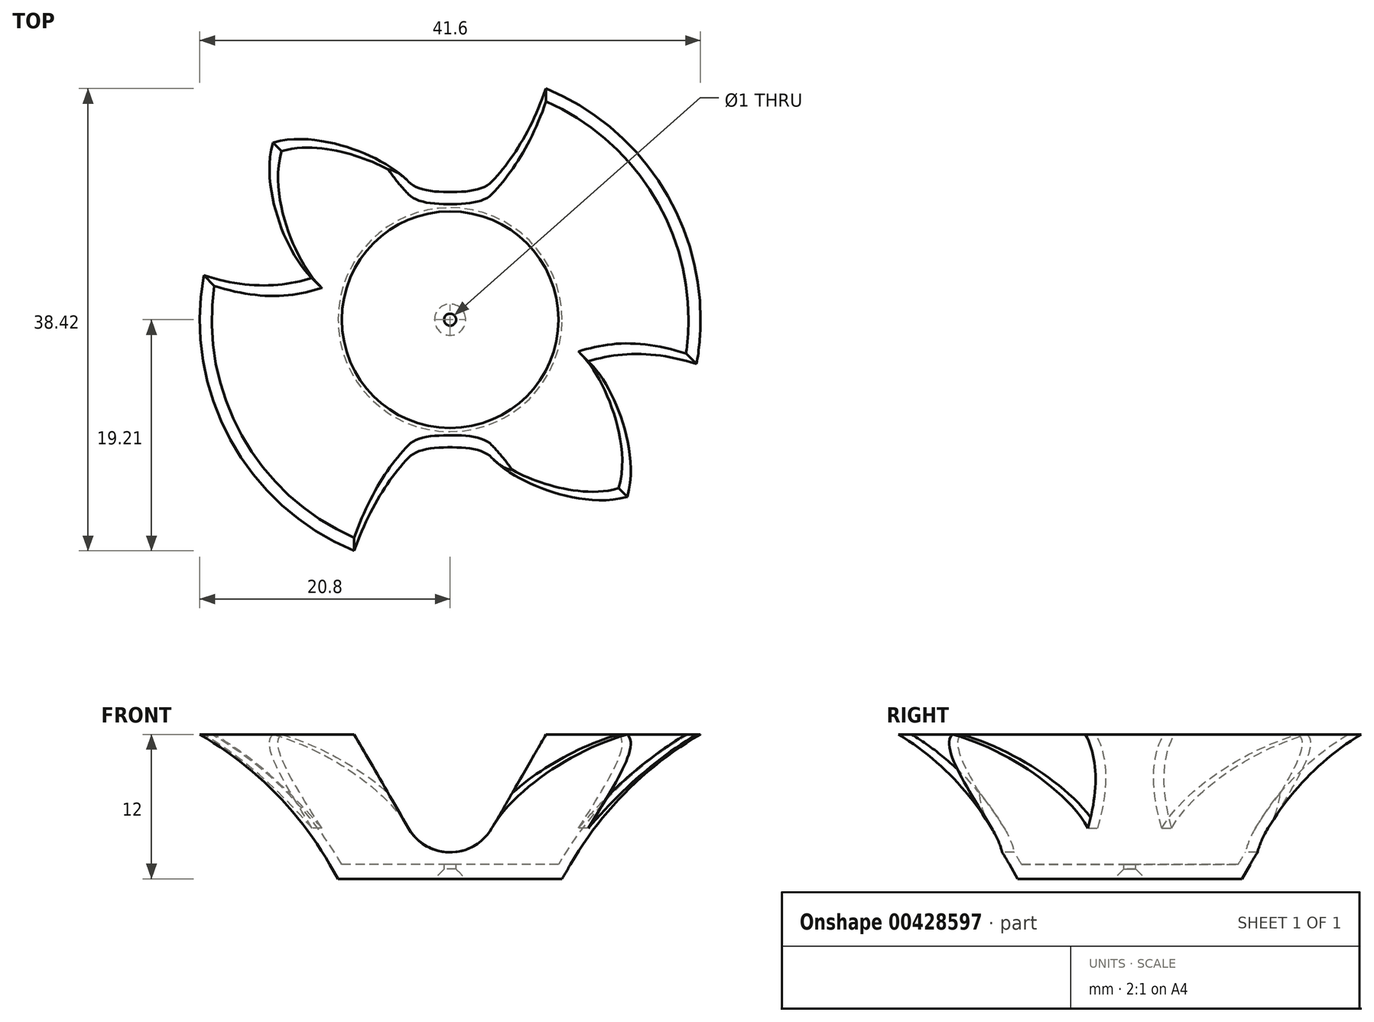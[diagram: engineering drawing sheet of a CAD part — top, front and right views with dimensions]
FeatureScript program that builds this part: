
annotation { "Feature Type Name" : "Feature", "Feature Type Description" : "" }
export const myFeature = defineFeature(function(context is Context, id is Id, definition is map)
    precondition{}
    {
        {
            var Q0;
            Q0=qCreatedBy(makeId("Front.planeOp"),FACE);
            var sketch = newSketch(context, id + "F0", { "sketchPlane" : qUnion([Q0])});
            skLineSegment(sketch, "E0", {"start": v(1.3, 0) * mm, "end": v(9.3, 0) * mm});
            skLineSegment(sketch, "E1", {"start": v(9.3, 0) * mm, "end": v(10, 1.2) * mm});
            skLineSegment(sketch, "E2", {"start": v(9, 1.2) * mm, "end": v(0.5, 1.2) * mm});
            skLineSegment(sketch, "E3", {"start": v(0.5, 1.2) * mm, "end": v(0.5, 0.8) * mm});
            skLineSegment(sketch, "E4", {"start": v(0.5, 0.8) * mm, "end": v(1.3, 0) * mm});
            skArc(sketch, "E5", {"start": v(20.8, 12) * mm, "mid": v(14.69, 7.31) * mm, "end": v(10, 1.2) * mm});
            skArc(sketch, "E6", {"start": v(19.8, 12) * mm, "mid": v(13.69, 7.31) * mm, "end": v(9, 1.2) * mm});
            skLineSegment(sketch, "E7", {"start": v(19.8, 12) * mm, "end": v(0, 0.57) * mm, "construction": true});
            skLineSegment(sketch, "E8", {"start": v(0, 0.57) * mm, "end": v(0, 0) * mm, "construction": true});
            skLineSegment(sketch, "E9", {"start": v(19.8, 12) * mm, "end": v(20.8, 12) * mm});
            skLineSegment(sketch, "E10", {"start": v(9, 1.2) * mm, "end": v(8.3, 0) * mm, "construction": true});
            skSolve(sketch);
        }
        {
            var Q0;
            Q0 = qSketchRegion(id + "F0", true);
            var Q1;
            Q1=sQuery(id+"F0.wireOp",EDGE,"E8");
            revolve(context, id + "F1", {"entities" : qUnion([Q0]), "axis" : qUnion([Q1]), "revolveType" : RevolveType.FULL});
        }
        {
            var Q0;
            Q0=qCreatedBy(makeId("Front.planeOp"),FACE);
            var sketch = newSketch(context, id + "F2", { "sketchPlane" : qUnion([Q0])});
            skArc(sketch, "E11", {"start": v(-3.46, 4.2) * mm, "mid": v(0, 2.2) * mm, "end": v(3.46, 4.2) * mm});
            skPoint(sketch, "E12", {"position": v(0, 12) * mm});
            skLineSegment(sketch, "E13", {"start": v(-3.46, 4.2) * mm, "end": v(-7.97, 12) * mm});
            skLineSegment(sketch, "E14", {"start": v(-7.97, 12) * mm, "end": v(7.97, 12) * mm});
            skLineSegment(sketch, "E15", {"start": v(7.97, 12) * mm, "end": v(3.46, 4.2) * mm});
            skSolve(sketch);
        }
        {
            var Q0;
            Q0 = qSketchRegion(id + "F2", true);
            extrude(context, id + "F3", {"entities" : qUnion([Q0]), "operationType" : NewBodyOperationType.REMOVE, "endBound" : BoundingType.THROUGH_ALL, "oppositeDirection" : true, "depth" : 25 * mm, "hasSecondDirection" : true, "secondDirectionBound" : SecondDirectionBoundingType.THROUGH_ALL, "secondDirectionOppositeDirection" : false, "secondDirectionDepth" : 25 * mm});
        }
        {
            var Q0;
            Q0=qCreatedBy(makeId("Front.planeOp"),FACE);
            var sketch = newSketch(context, id + "F4", { "sketchPlane" : qUnion([Q0])});
            skLineSegment(sketch, "E16", {"start": v(0, 0) * mm, "end": v(0, 50) * mm});
            skSolve(sketch);
        }
        {
            var Q0;
            Q0=sQuery(id+"F4.wireOp",EDGE,"E16");
            var Q1;
            Q1=qCreatedBy(makeId("Front.planeOp"),FACE);
            cPlane(context, id + "F5", {"entities" : qUnion([Q0, Q1]), "cplaneType" : CPlaneType.LINE_ANGLE, "offset" : 25 * mm, "angle" : 45 * degree, "width" : 150 * mm, "height" : 150 * mm});
        }
        {
            var Q0;
            Q0=qCreatedBy(id+"F5.planeOp",FACE);
            var sketch = newSketch(context, id + "F6", { "sketchPlane" : qUnion([Q0])});
            skArc(sketch, "E17", {"start": v(0, 12) * mm, "mid": v(-4.15, 9.06) * mm, "end": v(-5.66, 4.2) * mm});
            skArc(sketch, "E18", {"start": v(5.66, 4.2) * mm, "mid": v(4.15, 9.06) * mm, "end": v(0, 12) * mm});
            skLineSegment(sketch, "E19", {"start": v(5.66, 4.2) * mm, "end": v(15, 15.94) * mm});
            skLineSegment(sketch, "E20", {"start": v(15, 15.94) * mm, "end": v(0, 15.94) * mm});
            skLineSegment(sketch, "E21", {"start": v(0, 15.94) * mm, "end": v(-15, 15.94) * mm});
            skLineSegment(sketch, "E22", {"start": v(-15, 15.94) * mm, "end": v(-5.66, 4.2) * mm});
            skSolve(sketch);
        }
        {
            var Q0;
            Q0 = qSketchRegion(id + "F6", true);
            extrude(context, id + "F7", {"entities" : qUnion([Q0]), "operationType" : NewBodyOperationType.REMOVE, "endBound" : BoundingType.THROUGH_ALL, "oppositeDirection" : true, "depth" : 25 * mm, "hasSecondDirection" : true, "secondDirectionBound" : SecondDirectionBoundingType.THROUGH_ALL, "secondDirectionOppositeDirection" : false, "secondDirectionDepth" : 25 * mm});
        }
    });
